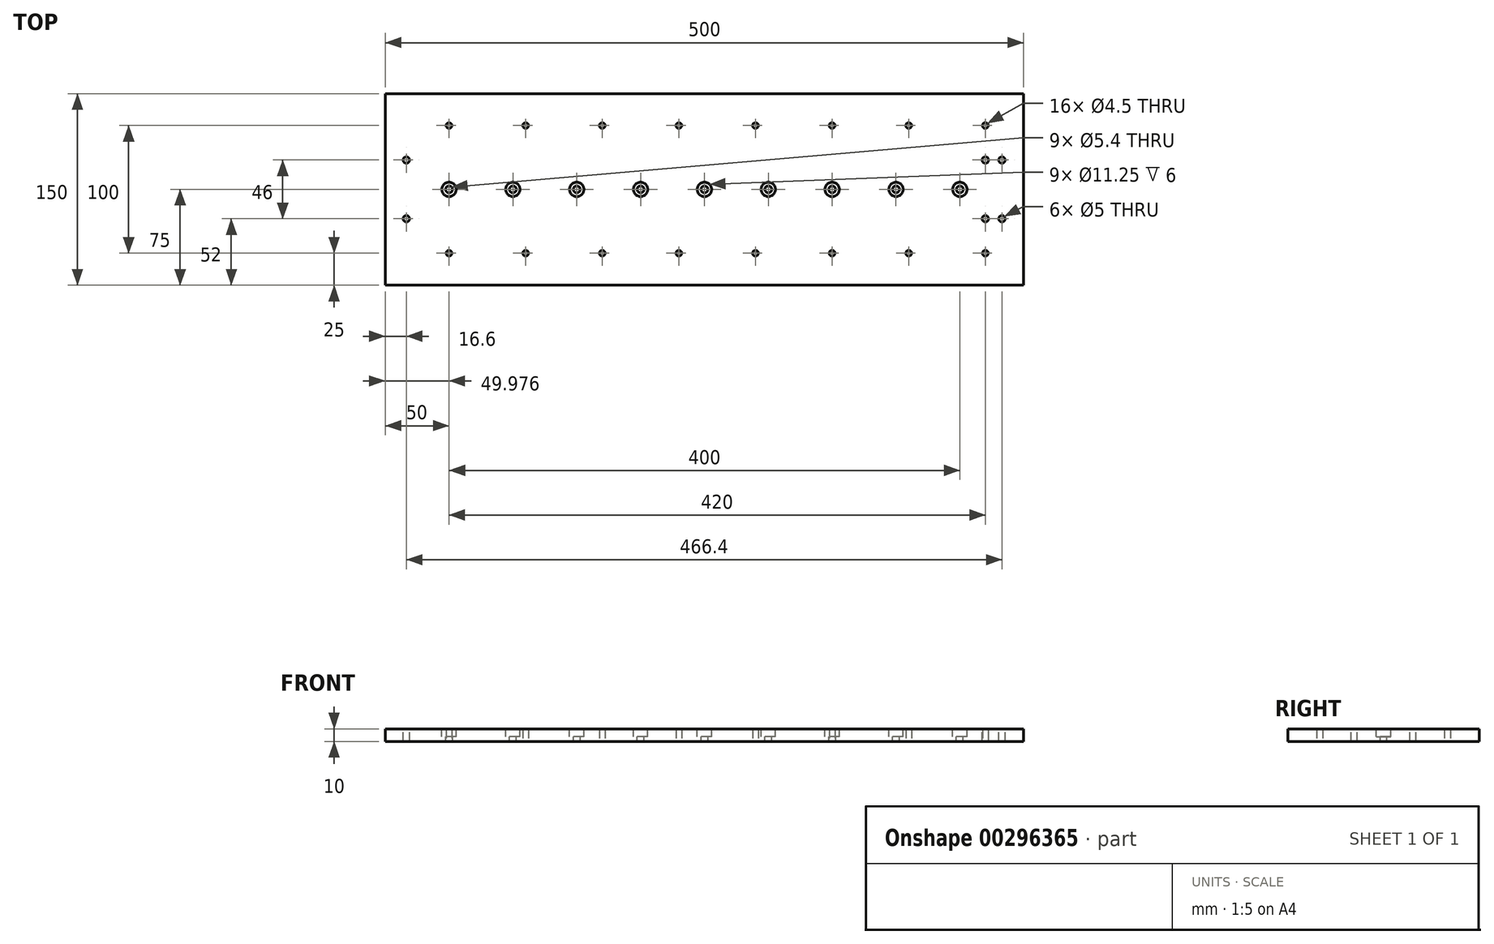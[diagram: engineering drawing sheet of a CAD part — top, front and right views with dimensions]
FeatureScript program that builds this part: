
annotation { "Feature Type Name" : "Feature", "Feature Type Description" : "" }
export const myFeature = defineFeature(function(context is Context, id is Id, definition is map)
    precondition{}
    {
        {
            var Q0;
            Q0=qCreatedBy(makeId("Top.planeOp"),FACE);
            var sketch = newSketch(context, id + "F0", { "sketchPlane" : qUnion([Q0])});
            skLineSegment(sketch, "E0.bottom", {"start": v(250, 75) * mm, "end": v(-250, 75) * mm});
            skLineSegment(sketch, "E0.top", {"start": v(250, -75) * mm, "end": v(-250, -75) * mm});
            skLineSegment(sketch, "E0.left", {"start": v(250, 75) * mm, "end": v(250, -75) * mm});
            skLineSegment(sketch, "E0.right", {"start": v(-250, 75) * mm, "end": v(-250, -75) * mm});
            skPoint(sketch, "E0.middle", {"position": v(0, 0) * mm});
            skLineSegment(sketch, "E1", {"start": v(-250, 0) * mm, "end": v(250, 0) * mm, "construction": true});
            skLineSegment(sketch, "E2", {"start": v(-250, 50) * mm, "end": v(250, 50) * mm, "construction": true});
            skLineSegment(sketch, "E3", {"start": v(-250, -50) * mm, "end": v(250, -50) * mm, "construction": true});
            skPoint(sketch, "E4", {"position": v(219.98, 50) * mm});
            skPoint(sketch, "E5.0.1.0", {"position": v(219.98, -50) * mm});
            skPoint(sketch, "E5.1.0.0", {"position": v(159.98, 50) * mm});
            skPoint(sketch, "E5.1.1.0", {"position": v(159.98, -50) * mm});
            skPoint(sketch, "E5.2.0.0", {"position": v(99.98, 50) * mm});
            skPoint(sketch, "E5.2.1.0", {"position": v(99.98, -50) * mm});
            skPoint(sketch, "E5.3.0.0", {"position": v(39.98, 50) * mm});
            skPoint(sketch, "E5.3.1.0", {"position": v(39.98, -50) * mm});
            skPoint(sketch, "E5.4.0.0", {"position": v(-20.02, 50) * mm});
            skPoint(sketch, "E5.4.1.0", {"position": v(-20.02, -50) * mm});
            skPoint(sketch, "E5.5.0.0", {"position": v(-80.02, 50) * mm});
            skPoint(sketch, "E5.5.1.0", {"position": v(-80.02, -50) * mm});
            skPoint(sketch, "E5.6.0.0", {"position": v(-140.02, 50) * mm});
            skPoint(sketch, "E5.6.1.0", {"position": v(-140.02, -50) * mm});
            skPoint(sketch, "E5.7.0.0", {"position": v(-200.02, 50) * mm});
            skPoint(sketch, "E5.7.1.0", {"position": v(-200.02, -50) * mm});
            skLineSegment(sketch, "E5.direction1", {"start": v(219.98, 50) * mm, "end": v(159.98, 50) * mm, "construction": true});
            skLineSegment(sketch, "E5.direction2", {"start": v(219.98, 50) * mm, "end": v(219.98, -50) * mm, "construction": true});
            skSolve(sketch);
        }
        {
            var Q0;
            Q0 = qSketchRegion(id + "F0", true);
            extrude(context, id + "F1", {"entities" : qUnion([Q0]), "depth" : 10 * mm});
        }
        {
            var Q0;
            Q0=sQuery(id+"F0.wireOp",VERTEX,"E4");
            var Q1;
            Q1=sQuery(id+"F0.wireOp",VERTEX,"E5.1.0.0");
            var Q2;
            Q2=sQuery(id+"F0.wireOp",VERTEX,"E5.2.0.0");
            var Q3;
            Q3=sQuery(id+"F0.wireOp",VERTEX,"E5.3.0.0");
            var Q4;
            Q4=sQuery(id+"F0.wireOp",VERTEX,"E5.4.0.0");
            var Q5;
            Q5=sQuery(id+"F0.wireOp",VERTEX,"E5.5.0.0");
            var Q6;
            Q6=sQuery(id+"F0.wireOp",VERTEX,"E5.6.0.0");
            var Q7;
            Q7=sQuery(id+"F0.wireOp",VERTEX,"E5.7.0.0");
            var Q8;
            Q8=sQuery(id+"F0.wireOp",VERTEX,"E5.7.1.0");
            var Q9;
            Q9=sQuery(id+"F0.wireOp",VERTEX,"E5.6.1.0");
            var Q10;
            Q10=sQuery(id+"F0.wireOp",VERTEX,"E5.5.1.0");
            var Q11;
            Q11=sQuery(id+"F0.wireOp",VERTEX,"E5.4.1.0");
            var Q12;
            Q12=sQuery(id+"F0.wireOp",VERTEX,"E5.3.1.0");
            var Q13;
            Q13=sQuery(id+"F0.wireOp",VERTEX,"E5.2.1.0");
            var Q14;
            Q14=sQuery(id+"F0.wireOp",VERTEX,"E5.1.1.0");
            var Q15;
            Q15=sQuery(id+"F0.wireOp",VERTEX,"E5.0.1.0");
            var Q16;
            Q16=makeQuery(id+"F1.opExtrude","SWEPT_BODY",BODY,{"disambiguationData":[OSD([sQuery(id+"F0.wireOp",EDGE,"E0.bottom"),sQuery(id+"F0.wireOp",EDGE,"E0.top"),sQuery(id+"F0.wireOp",EDGE,"E0.left"),sQuery(id+"F0.wireOp",EDGE,"E0.right")])]});
            hole(context, id + "F2", {"style" : HoleStyle.SIMPLE, "endStyle" : HoleEndStyle.THROUGH, "oppositeDirection" : true, "standardTappedOrClearance" : lookupTablePath({ "standard" : "ISO", "engagement" : "25%", "pitch" : "0.8 mm", "size" : "M5", "type" : "Tapped" }), "standardBlindInLast" : lookupTablePath({ "standard" : "ISO", "engagement" : "25%", "pitch" : "0.8 mm", "size" : "M5", "type" : "Tapped" }), "holeDiameter" : 4.5 * mm, "showTappedDepth" : true, "tappedDepth" : 8 * mm, "tapClearance" : 3, "locations" : qUnion([Q0, Q1, Q2, Q3, Q4, Q5, Q6, Q7, Q8, Q9, Q10, Q11, Q12, Q13, Q14, Q15]), "scope" : qUnion([Q16])});
        }
        {
            var Q0;
            Q0=makeQuery(id+"F1.opExtrude","CAP_FACE",FACE,{"disambiguationData":[OSD([sQuery(id+"F0.wireOp",EDGE,"E0.bottom"),sQuery(id+"F0.wireOp",EDGE,"E0.top"),sQuery(id+"F0.wireOp",EDGE,"E0.left"),sQuery(id+"F0.wireOp",EDGE,"E0.right")])],"isStart":false});
            var sketch = newSketch(context, id + "F3", { "sketchPlane" : qUnion([Q0])});
            skLineSegment(sketch, "E6", {"start": v(-250, 0) * mm, "end": v(250, 0) * mm, "construction": true});
            skPoint(sketch, "E7", {"position": v(200, 0) * mm});
            skPoint(sketch, "E8.1.0.0", {"position": v(150, 0) * mm});
            skPoint(sketch, "E8.2.0.0", {"position": v(100, 0) * mm});
            skPoint(sketch, "E8.3.0.0", {"position": v(50, 0) * mm});
            skPoint(sketch, "E8.4.0.0", {"position": v(0, 0) * mm});
            skPoint(sketch, "E8.5.0.0", {"position": v(-50, 0) * mm});
            skPoint(sketch, "E8.6.0.0", {"position": v(-100, 0) * mm});
            skPoint(sketch, "E8.7.0.0", {"position": v(-150, 0) * mm});
            skPoint(sketch, "E8.8.0.0", {"position": v(-200, 0) * mm});
            skLineSegment(sketch, "E8.direction1", {"start": v(200, 0) * mm, "end": v(150, 0) * mm, "construction": true});
            skSolve(sketch);
        }
        {
            var Q0;
            Q0=sQuery(id+"F3.wireOp",VERTEX,"E7");
            var Q1;
            Q1=sQuery(id+"F3.wireOp",VERTEX,"E8.1.0.0");
            var Q2;
            Q2=sQuery(id+"F3.wireOp",VERTEX,"E8.2.0.0");
            var Q3;
            Q3=sQuery(id+"F3.wireOp",VERTEX,"E8.3.0.0");
            var Q4;
            Q4=sQuery(id+"F3.wireOp",VERTEX,"E8.4.0.0");
            var Q5;
            Q5=sQuery(id+"F3.wireOp",VERTEX,"E8.5.0.0");
            var Q6;
            Q6=sQuery(id+"F3.wireOp",VERTEX,"E8.6.0.0");
            var Q7;
            Q7=sQuery(id+"F3.wireOp",VERTEX,"E8.7.0.0");
            var Q8;
            Q8=sQuery(id+"F3.wireOp",VERTEX,"E8.8.0.0");
            var Q9;
            Q9=makeQuery(id+"F1.opExtrude","SWEPT_BODY",BODY,{"disambiguationData":[OSD([sQuery(id+"F0.wireOp",EDGE,"E0.bottom"),sQuery(id+"F0.wireOp",EDGE,"E0.top"),sQuery(id+"F0.wireOp",EDGE,"E0.left"),sQuery(id+"F0.wireOp",EDGE,"E0.right")])]});
            hole(context, id + "F4", {"style" : HoleStyle.C_BORE, "endStyle" : HoleEndStyle.THROUGH, "standardTappedOrClearance" : lookupTablePath({ "standard" : "ISO", "engagement" : "25%", "pitch" : "1 mm", "size" : "M6", "type" : "Tapped" }), "standardBlindInLast" : lookupTablePath({ "standard" : "ISO", "engagement" : "25%", "pitch" : "1 mm", "size" : "M6", "type" : "Tapped" }), "holeDiameter" : 5.4 * mm, "cBoreDiameter" : 11.25 * mm, "cBoreDepth" : 6 * mm, "showTappedDepth" : true, "tappedDepth" : 8 * mm, "tapClearance" : 3, "locations" : qUnion([Q0, Q1, Q2, Q3, Q4, Q5, Q6, Q7, Q8]), "scope" : qUnion([Q9])});
        }
        {
            var Q0;
            Q0=makeQuery(id+"F1.opExtrude","CAP_FACE",FACE,{"disambiguationData":[OSD([sQuery(id+"F0.wireOp",EDGE,"E0.bottom"),sQuery(id+"F0.wireOp",EDGE,"E0.top"),sQuery(id+"F0.wireOp",EDGE,"E0.left"),sQuery(id+"F0.wireOp",EDGE,"E0.right")])],"isStart":false});
            var sketch = newSketch(context, id + "F5", { "sketchPlane" : qUnion([Q0])});
            skLineSegment(sketch, "E9", {"start": v(-233.4, 23) * mm, "end": v(-233.4, -23) * mm, "construction": true});
            skLineSegment(sketch, "E10", {"start": v(220, 23) * mm, "end": v(220, -23) * mm, "construction": true});
            skLineSegment(sketch, "E11", {"start": v(233, 23) * mm, "end": v(233, -23) * mm, "construction": true});
            skPoint(sketch, "E12", {"position": v(-233.4, 23) * mm});
            skPoint(sketch, "E13", {"position": v(-233.4, -23) * mm});
            skPoint(sketch, "E14", {"position": v(220, 23) * mm});
            skPoint(sketch, "E15", {"position": v(220, -23) * mm});
            skPoint(sketch, "E16", {"position": v(233, -23) * mm});
            skPoint(sketch, "E17", {"position": v(233, 23) * mm});
            skSolve(sketch);
        }
        {
            var Q0;
            Q0=sQuery(id+"F5.wireOp",VERTEX,"E12");
            var Q1;
            Q1=sQuery(id+"F5.wireOp",VERTEX,"E13");
            var Q2;
            Q2=sQuery(id+"F5.wireOp",VERTEX,"E14");
            var Q3;
            Q3=sQuery(id+"F5.wireOp",VERTEX,"E17");
            var Q4;
            Q4=sQuery(id+"F5.wireOp",VERTEX,"E15");
            var Q5;
            Q5=sQuery(id+"F5.wireOp",VERTEX,"E16");
            var Q6;
            Q6=makeQuery(id+"F1.opExtrude","SWEPT_BODY",BODY,{"disambiguationData":[OSD([sQuery(id+"F0.wireOp",EDGE,"E0.bottom"),sQuery(id+"F0.wireOp",EDGE,"E0.top"),sQuery(id+"F0.wireOp",EDGE,"E0.left"),sQuery(id+"F0.wireOp",EDGE,"E0.right")])]});
            hole(context, id + "F6", {"style" : HoleStyle.SIMPLE, "endStyle" : HoleEndStyle.THROUGH, "standardTappedOrClearance" : lookupTablePath({ "standard" : "ISO", "engagement" : "75%", "pitch" : "1 mm", "size" : "M6", "type" : "Tapped" }), "standardBlindInLast" : lookupTablePath({ "standard" : "ISO", "engagement" : "75%", "pitch" : "1 mm", "size" : "M6", "type" : "Tapped" }), "holeDiameter" : 5 * mm, "showTappedDepth" : true, "tappedDepth" : 9.6 * mm, "tapClearance" : 3, "locations" : qUnion([Q0, Q1, Q2, Q3, Q4, Q5]), "scope" : qUnion([Q6]), "majorDiameter" : 6 * mm});
        }
    });
